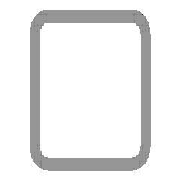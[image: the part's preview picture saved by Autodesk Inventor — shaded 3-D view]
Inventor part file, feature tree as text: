
AUTODESK INVENTOR PART (.ipt)
format: ipt  version: 2025.3 (Build 293356030, 356C)  size: 143,360 bytes
history: native  units: mm (DEFAULTED — no unit token found)
features: other x4, plane x2, split x1, sketch x1
ambient origin geometry x8: Origin, YZ Plane, XZ Plane, XY Plane, X Axis, Y Axis, Z Axis, Center Point
bodies: Solid1 (feature_tree), Body (feature_tree)
feature tree (8):
  parser-record x1  (decoder bookkeeping rows leaked as tree rows — omitted from the tree; the rows remain in map.json)
  other  "Driven Length"
  other  "Start Plane"
  other  "End Plane"
  plane  "Work Plane4"
  split  "Split1"
  sketch  "Sketch3"  dims[d3=2366.612931mm d4=0.0mm d7=6.0mm d9=80.0mm d11=80.0mm d12=3.0mm d13=80.0mm d14=2446.612931mm d15=40.0mm d16=40.0mm d17=90.0deg d18=2366.612931mm]
  plane  "Work Plane3"
